# Revit family: ShowerMixer_Square_Ss3_Thermostatic_Vitra_AquaHeatSeries-A47160
name_source: partatom
category: Plumbing Fixtures
revit_build: Autodesk Revit 2017 (Build: 20160225_1515(x64)
units: mm (PartAtom-declared; Revit-internal decimal feet)

## family parameters
Always vertical = No
Cut with Voids When Loaded = No
OmniClass Number = 23.45.55.17
OmniClass Title = Mixing Faucets
Part Type = Normal
Room Calculation Point = No
Round Connector Dimension = Use Diameter
Shared = Yes
Work Plane-Based = No

## types (3) — shared parameters
BIMobject category = Bath/Shower Mixer
CW Connection = Yes
Coating Material = Chrome
Color = Chrome
Connection Diameter (mm) = 15 mm  [stored 0.0492126 ft]
Depth(mm) = 112 mm  [stored 0.367454 ft]
Description = Shower Mixer - Thermostatic - Square
Design country = Turkey
HW Connection = Yes
Height(mm) = 78 mm  [stored 0.255906 ft]
Hot Water Supply (max.) = 80 °C
Hot Water temperature, factory set to = 38 °C
IFC Classification = Sanitary Terminal
Main Material = Brass
Manufacturer = Vitra
Manufacturer name = Vitra
Masterformat 2014 Code = 22 40 00
Masterformat 2014 Description = Plumbing Fixtures
Min. flow pressure of = 0.5 bar
MountingType = Wall Mounted
NBS Referans Code = 45-35-70/315
NBS Referans Description = Water supply fittings for baths
Nominal height = 0.000
Nominal width = 0.000
Number Of Connections = 2 mm  [stored 0.00656168 ft]
OmniClass Code = 23.45.55.17
OmniClass Description = Mixing Faucets
Product Properties = Water Saving
Product Type = Shower Mixer
Product certification = https://vitraglobal.com
Product family = AquaHeat
Product group = AquaHeat Shower Mixer
Range of Hot Water Supply = 5 - 65 °C
Range of flow pressure = 1 - 5 bar
Test Pressure = 16 bar
UNSPSC Code = 301815
URL = https://vitraglobal.com
Uniclass 1.4 Code = L725111
Uniclass 1.4 Description = Mixer taps
Uniclass 2.0 Code = Pr_40_20_87_09
Uniclass 2.0 Description = Bath taps
Uniclass 2015 Code = Pr_40_20_87_09
Uniclass 2015 Name = Bath taps
Uniformat II Code = 22 40 00
Uniformat II Description = Plumbing Fixture
Weight Net (kg) = 3,100
Width(mm) = 295 mm  [stored 0.967848 ft]
Youtube = https://www.youtube.com
zero-valued in all types: Cost

## per-type parameters (varying)
| type | Article No. (default) | Brand | Model | Product SKU | Product data url | Technical description | Warranty Period (Year) |
| ShowerMixer_Square_Ss3_Thermostatic_Vitra_AquaHeatSeries-A47160 | A47160 | Artema | A47160 | A47160 | https://www.vitra.com.tr | https://www.vitra.com.tr | 10 Years |
| ShowerMixer_Square_Ss3_Thermostatic_Vitra_AquaHeatSeries-A47160EKM | A47160EKM | VitrA | A47160EKM | A47160EKM | https://www.vitra-bad.fr | http://cdn.vitra.com.tr | 7 Years |
| ShowerMixer_Square_Ss3_Thermostatic_Vitra_AquaHeatSeries-A47160EXP | A47160EXP | VitrA | A47160EXP | A47160EXP | https://www.vitra-bad.fr | http://cdn.vitra.com.tr | 7 Years |

note: [stored X ft] marks values corroborated as IEEE doubles in the binary element streams (Revit-internal decimal feet)

## geometry (parser evidence)
native form markers: Sweep x2
no freeform markers — native parametric forms only
